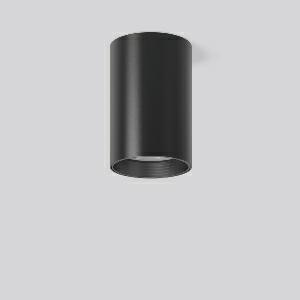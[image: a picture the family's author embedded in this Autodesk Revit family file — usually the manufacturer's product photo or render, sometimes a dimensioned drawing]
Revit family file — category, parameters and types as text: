
# Revit family: heledon_maxi_a_931227_003_2_76_35d7
name_source: partatom
category: Lighting Fixtures
units: mm (PartAtom-declared; Revit-internal decimal feet)

## family parameters
Cut with Voids When Loaded = No
Host = Face
Light Source = No
Part Type = Normal
Room Calculation Point = No
Round Connector Dimension = Use Diameter
Shared = No

## types (1)
- HELEDON maxi A (1 x LED Modul 927, 3500 lm, 2700)
    Apparent Load = 35 VA
    Approval mark = CE
    CIE Flux Codes = 97 100 100 100 100
    Color Rendering = 92
    Color Temperature = 2700
    Default Elevation = 1800 mm
    Description = Series: HELEDON maxi
Cylindrical surface-mounted downlight. Housing: die-cast aluminium, powder-coated. Internal ceiling frame polycarbonate with bayonet mounting. Black plastic ring and recessed LED to prevent glare from the side. Optical assembly with lens made of plastic (polycarbonate) for the best homogeneous light distribution - can be changed without tools. Best colour rendering index Ra>90. Suitable for Ceiling mounting. Easy installation with a separate ceiling frame with bayonet mounting and plug connection. Driver integrated. Connected via plug-in connector. High quality converter without flickering and stroboscopic effect. The following accessories can be mounted without use of tools: interchangeable lenses, decorative glasses, honeycomb louvre, clear and frosted diffusers, white interchangeable plastic ring. 
Colour: deep black, matt (RAL 9005)
Diameter: 123 mm
Height: 183 mm
Lamp: LED
Socket: without socket
Colour temperature: 2700K
Colour rendering index (CRI): 92
System power: 35 W
Rated luminous flux: 3500 lm
Luminous efficiency: 100 lm/W
Control gear: Converter, dimmable, DALI
Protection class: I
Type of protection: IP 20
    Height = 183 mm
    Lamp = 1 x LED Modul 927
    Lamp Light Flux = 3500 lm
    Lamp count = 1
    Length = 123 mm
    Lifetime = 50000 h
    Luminous efficacy = 100 lm/W
    Manufacturer = RZB
    ModVariant = No
    Model = 931227.003.2.76
    Mounting Place = Ceiling
    Mounting Type = Surface mounted
    Number of Poles = 1
    OnlyDefault = Yes
    Power Factor = 1
    Product Name = HELEDON maxi A
    Product group = Surface mounted downlights
    ProductGroupID = 302
    Protection Class = Protection class I
    Protection Degree = IP 20
    RLX_Detail_Level = 1
    RLX_Emergency_Light_Flux = 0 lm
    RLX_Emergency_Type = 0
    RLX_Emergency_Type_DB = No
    RlxData = <blob elided: 97261 chars, md5=a6582fe9>
    Socket = socket
    Standby Power = 0 W
    System Light Flux = 3500 lm
    System Power = 35 W
    Type Comments = Product without accessories
    Type Image = 931193.003.jpg
    URL = http://relux.com
    VarID = ---
    Voltage = 230 V
    Voltage Range = 220-240 V
    Weight = 0.00 kg
    Width = 0 mm  [stored 0 ft]

note: [stored X ft] marks values corroborated as IEEE doubles in the binary element streams (Revit-internal decimal feet)

## geometry (parser evidence)
native form markers: Blend x4, Sweep x11
no freeform markers — native parametric forms only
